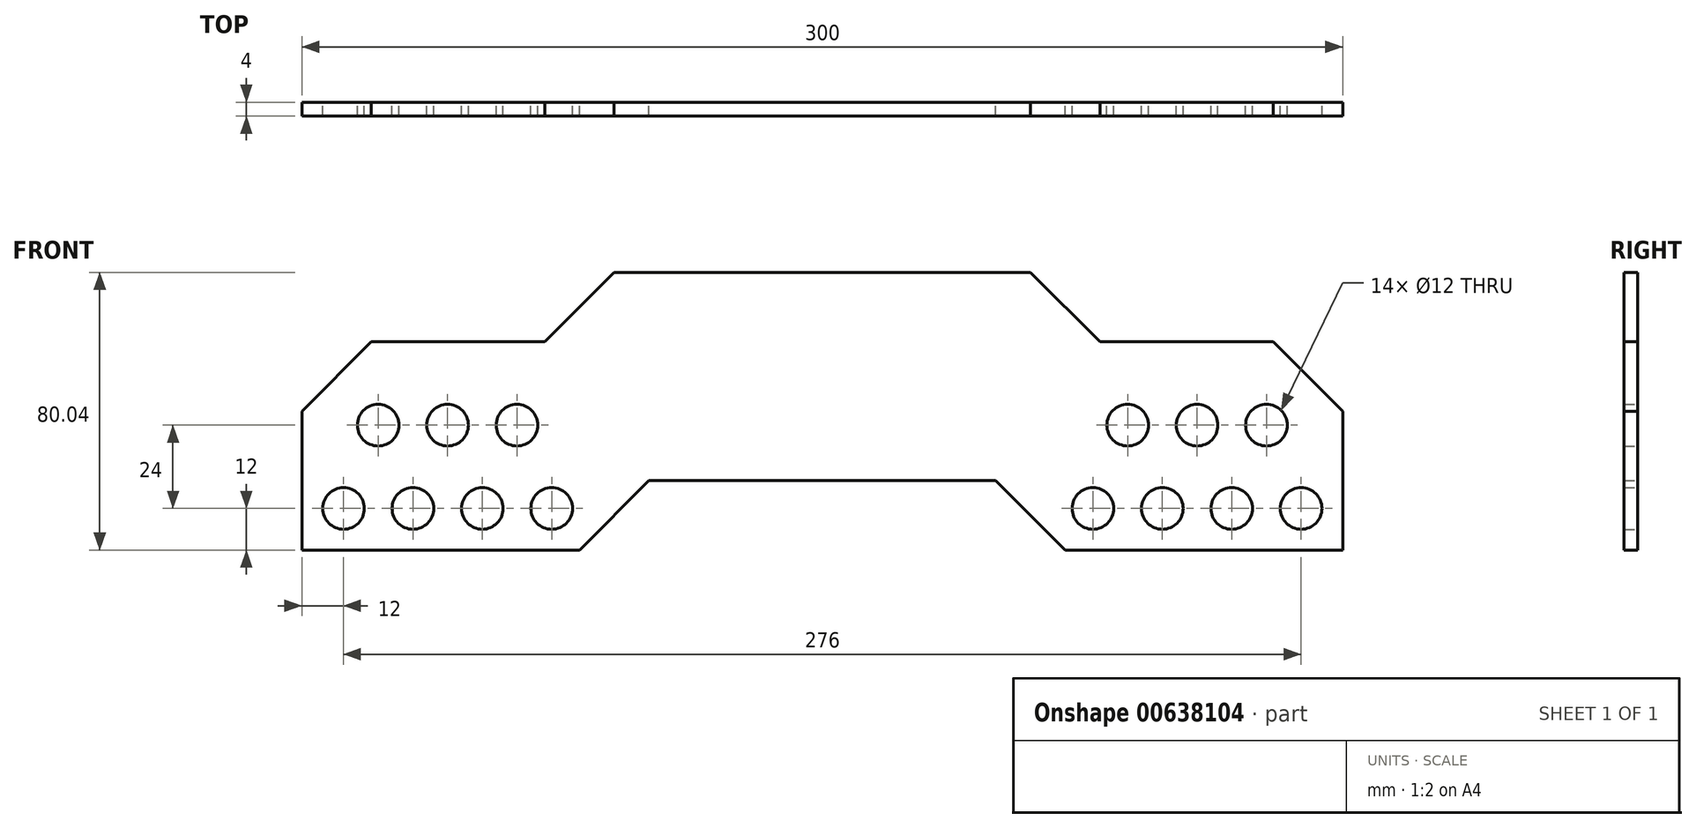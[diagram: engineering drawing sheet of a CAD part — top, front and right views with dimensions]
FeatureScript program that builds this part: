
annotation { "Feature Type Name" : "Feature", "Feature Type Description" : "" }
export const myFeature = defineFeature(function(context is Context, id is Id, definition is map)
    precondition{}
    {
        {
            var Q0;
            Q0=qCreatedBy(makeId("Front.planeOp"),FACE);
            var sketch = newSketch(context, id + "F0", { "sketchPlane" : qUnion([Q0])});
            skLineSegment(sketch, "E0", {"start": v(-80, 60.04) * mm, "end": v(-129.96, 60.04) * mm});
            skLineSegment(sketch, "E1", {"start": v(-129.96, 60.04) * mm, "end": v(-150, 40) * mm});
            skLineSegment(sketch, "E2", {"start": v(-150, 40) * mm, "end": v(-150, 0) * mm});
            skLineSegment(sketch, "E3", {"start": v(-150, 0) * mm, "end": v(-70, 0) * mm});
            skLineSegment(sketch, "E4", {"start": v(-70, 0) * mm, "end": v(-50, 20) * mm});
            skLineSegment(sketch, "E5", {"start": v(-50, 20) * mm, "end": v(0, 20) * mm});
            skLineSegment(sketch, "E6", {"start": v(-80, 60.04) * mm, "end": v(-60, 80.04) * mm});
            skLineSegment(sketch, "E7", {"start": v(0, 80.04) * mm, "end": v(-60, 80.04) * mm});
            skLineSegment(sketch, "E8.MirrorCS", {"start": v(0, 80.04) * mm, "end": v(60, 80.04) * mm});
            skLineSegment(sketch, "E9.MirrorCS", {"start": v(80, 60.04) * mm, "end": v(129.96, 60.04) * mm});
            skLineSegment(sketch, "E10.MirrorCS", {"start": v(129.96, 60.04) * mm, "end": v(150, 40) * mm});
            skLineSegment(sketch, "E11.MirrorCS", {"start": v(150, 40) * mm, "end": v(150, 0) * mm});
            skLineSegment(sketch, "E12.MirrorCS", {"start": v(150, 0) * mm, "end": v(70, 0) * mm});
            skLineSegment(sketch, "E13.MirrorCS", {"start": v(70, 0) * mm, "end": v(50, 20) * mm});
            skLineSegment(sketch, "E14.MirrorCS", {"start": v(50, 20) * mm, "end": v(0, 20) * mm});
            skLineSegment(sketch, "E15.MirrorCS", {"start": v(80, 60.04) * mm, "end": v(60, 80.04) * mm});
            skCircle(sketch, "E16", {"center": v(-138, 12) * mm, "radius": 6 * mm});
            skCircle(sketch, "E17", {"center": v(-118, 12) * mm, "radius": 6 * mm});
            skCircle(sketch, "E18", {"center": v(-98, 12) * mm, "radius": 6 * mm});
            skCircle(sketch, "E19", {"center": v(-78, 12) * mm, "radius": 6 * mm});
            skLineSegment(sketch, "E20", {"start": v(-138, 12) * mm, "end": v(-118, 12) * mm, "construction": true});
            skLineSegment(sketch, "E21", {"start": v(-98, 12) * mm, "end": v(-78, 12) * mm, "construction": true});
            skLineSegment(sketch, "E22", {"start": v(-118, 12) * mm, "end": v(-98, 12) * mm, "construction": true});
            skCircle(sketch, "E23", {"center": v(-128, 36) * mm, "radius": 6 * mm});
            skCircle(sketch, "E24", {"center": v(-108, 36) * mm, "radius": 6 * mm});
            skCircle(sketch, "E25", {"center": v(-88, 36) * mm, "radius": 6 * mm});
            skLineSegment(sketch, "E26", {"start": v(-128, 36) * mm, "end": v(-108, 36) * mm, "construction": true});
            skLineSegment(sketch, "E27", {"start": v(-108, 36) * mm, "end": v(-88, 36) * mm, "construction": true});
            skCircle(sketch, "E28.MirrorC", {"center": v(88, 36) * mm, "radius": 6 * mm});
            skCircle(sketch, "E29.MirrorC", {"center": v(108, 36) * mm, "radius": 6 * mm});
            skCircle(sketch, "E30.MirrorC", {"center": v(138, 12) * mm, "radius": 6 * mm});
            skCircle(sketch, "E31.MirrorC", {"center": v(118, 12) * mm, "radius": 6 * mm});
            skCircle(sketch, "E32.MirrorC", {"center": v(98, 12) * mm, "radius": 6 * mm});
            skCircle(sketch, "E33.MirrorC", {"center": v(78, 12) * mm, "radius": 6 * mm});
            skCircle(sketch, "E34.MirrorC", {"center": v(128, 36) * mm, "radius": 6 * mm});
            skSolve(sketch);
        }
        {
            var Q0;
            Q0=makeQuery(id+"F0.imprint","IMPRINT",FACE,{"disambiguationData":[TD([[makeQuery(id+"F0.imprint","IMPRINT",EDGE,{"derivedFrom":sQuery(id+"F0.wireOp",EDGE,"E0")}),1.0]])]});
            extrude(context, id + "F1", {"entities" : qUnion([Q0]), "depth" : 4 * mm, "offsetDistance" : 25 * mm});
        }
    });
